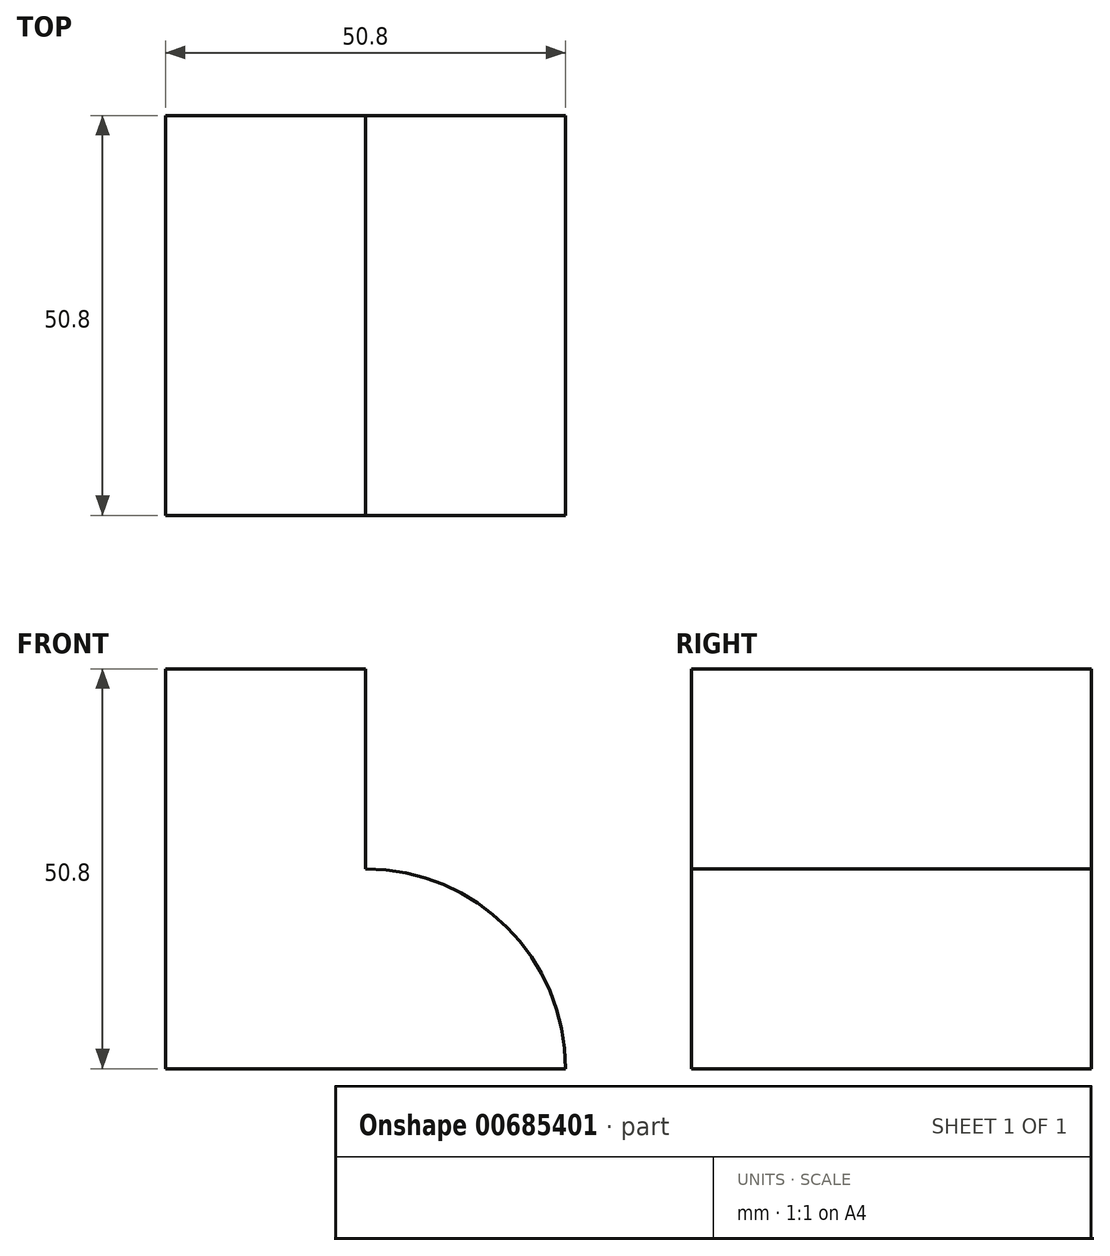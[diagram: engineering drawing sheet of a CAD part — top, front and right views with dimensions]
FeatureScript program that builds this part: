
annotation { "Feature Type Name" : "Feature", "Feature Type Description" : "" }
export const myFeature = defineFeature(function(context is Context, id is Id, definition is map)
    precondition{}
    {
        {
            var Q0;
            Q0=qCreatedBy(makeId("Front.planeOp"),FACE);
            var sketch = newSketch(context, id + "F0", { "sketchPlane" : qUnion([Q0])});
            skLineSegment(sketch, "E0", {"start": v(0, 0) * mm, "end": v(-50.8, 0) * mm});
            skLineSegment(sketch, "E1", {"start": v(-50.8, 0) * mm, "end": v(-50.8, 50.8) * mm});
            skLineSegment(sketch, "E2", {"start": v(-50.8, 50.8) * mm, "end": v(0, 50.8) * mm});
            skLineSegment(sketch, "E3", {"start": v(0, 50.8) * mm, "end": v(0, 0) * mm});
            skSolve(sketch);
        }
        {
            var Q0;
            Q0=makeQuery(id+"F0.imprint","IMPRINT",FACE,{"disambiguationData":[TD([[makeQuery(id+"F0.imprint","IMPRINT",EDGE,{"derivedFrom":sQuery(id+"F0.wireOp",EDGE,"E0")}),-1.0]])]});
            extrude(context, id + "F1", {"entities" : qUnion([Q0]), "depth" : 50.8 * mm, "offsetDistance" : 25.4 * mm});
        }
        {
            var Q0;
            Q0=makeQuery(id+"F1.opExtrude","CAP_FACE",FACE,{"disambiguationData":[OSD([sQuery(id+"F0.wireOp",EDGE,"E0"),sQuery(id+"F0.wireOp",EDGE,"E1"),sQuery(id+"F0.wireOp",EDGE,"E2"),sQuery(id+"F0.wireOp",EDGE,"E3")])],"isStart":false});
            var sketch = newSketch(context, id + "F2", { "sketchPlane" : qUnion([Q0])});
            skLineSegment(sketch, "E4", {"start": v(-25.4, 50.8) * mm, "end": v(-25.4, 25.4) * mm});
            skArc(sketch, "E5", {"start": v(0, 0) * mm, "mid": v(-7.44, 17.96) * mm, "end": v(-25.4, 25.4) * mm});
            skSolve(sketch);
        }
        {
            var Q0;
            {var subQ0=sQuery(id+"F2.wireOp",EDGE,"E4");Q0=makeQuery(id+"F2.imprint","IMPRINT",FACE,{"disambiguationData":[TD([[makeQuery(id+"F2.imprint","IMPRINT",EDGE,{"derivedFrom":subQ0}),1.0]])]});}
            extrude(context, id + "F3", {"entities" : qUnion([Q0]), "operationType" : NewBodyOperationType.REMOVE, "oppositeDirection" : true, "depth" : 50.8 * mm, "offsetDistance" : 25.4 * mm});
        }
    });
